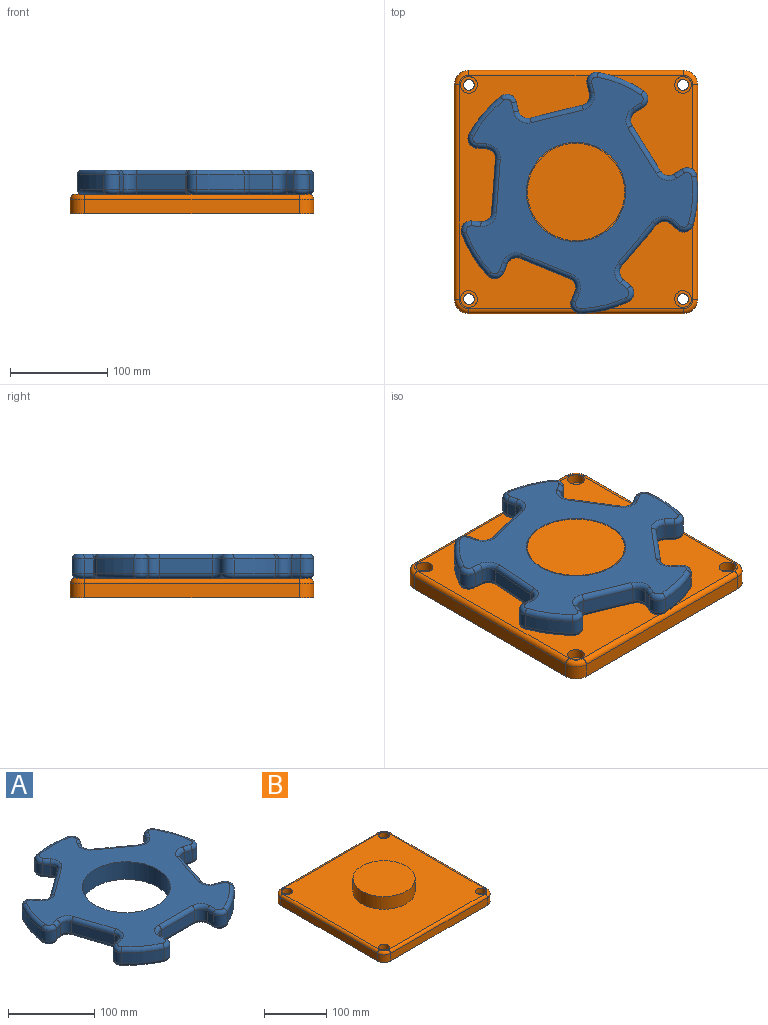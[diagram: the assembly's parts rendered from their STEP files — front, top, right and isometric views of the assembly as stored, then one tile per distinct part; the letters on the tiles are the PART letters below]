
ASSEMBLY  parts=2 mates=1
PART A: 123 faces, bbox 268.9x258.5x25 mm
  f0: plane 238.57x229.73mm, normal (0,0,1), area 21505.7mm2, adj f6,f43,f44,f45,f46,f47,f48,f49
  f1: plane 238.57x229.73mm, normal (0,0,-1), area 21505.7mm2, adj f6,f83,f84,f85,f86,f87,f88,f89
  f2: cylinder r=125mm len=40.68mm, axis (0,0,-1), area 759.5mm2, adj f13,f42,f51,f91
  f3: cylinder r=125mm len=47.82mm, axis (0,0,-1), area 759.5mm2, adj f35,f41,f67,f107
  f4: cylinder r=125mm len=50.29mm, axis (0,0,-1), area 759.5mm2, adj f28,f34,f82,f122
  f5: cylinder r=125mm len=47.82mm, axis (0,0,-1), area 759.5mm2, adj f21,f27,f66,f106
  f6: cylinder r=51mm len=102mm, axis (0,0,-1), area 8011.1mm2, adj f0,f1
  f7: cylinder r=125mm len=40.68mm, axis (0,0,-1), area 759.5mm2, adj f14,f20,f50,f90
  f8: plane 15x9.73mm, normal (-1,0,0), area 146mm2, adj f11,f14,f46,f86
  f9: plane 55x15mm, normal (0,-1,0), area 825mm2, adj f11,f12,f43,f83
  f10: plane 15x9.73mm, normal (1,0,0), area 146mm2, adj f12,f13,f47,f87
  f11: cylinder r=10mm len=15mm, axis (0,0,-1), area 235.6mm2, adj f8,f9,f44,f84
  f12: cylinder r=10mm len=15mm, axis (0,0,-1), area 235.6mm2, adj f9,f10,f45,f85
  f13: cylinder r=10mm len=15mm, axis (0,0,-1), area 299.5mm2, adj f2,f10,f49,f89
  f14: cylinder r=10mm len=15mm, axis (0,0,-1), area 299.5mm2, adj f7,f8,f48,f88
  f15: plane 15x9.26mm, normal (-0.31,-0.95,0), area 146mm2, adj f18,f21,f62,f102
  f16: plane 52.31x17mm, normal (0.95,-0.31,0), area 825mm2, adj f18,f19,f58,f98
  f17: plane 15x9.26mm, normal (0.31,0.95,0), area 146mm2, adj f19,f20,f54,f94
  f18: cylinder r=10mm len=15mm, axis (0,0,-1), area 235.6mm2, adj f15,f16,f60,f100
  f19: cylinder r=10mm len=15mm, axis (0,0,-1), area 235.6mm2, adj f16,f17,f56,f96
  f20: cylinder r=10mm len=16.25mm, axis (0,0,-1), area 299.5mm2, adj f7,f17,f52,f92
  f21: cylinder r=10mm len=15mm, axis (0,0,-1), area 299.5mm2, adj f5,f15,f64,f104
  f22: plane 15x7.87mm, normal (0.81,-0.59,0), area 146mm2, adj f25,f28,f78,f118
  f23: plane 44.5x32.33mm, normal (0.59,0.81,0), area 825mm2, adj f25,f26,f74,f114
  f24: plane 15x7.87mm, normal (-0.81,0.59,0), area 146mm2, adj f26,f27,f70,f110
  f25: cylinder r=10mm len=15mm, axis (0,0,-1), area 235.6mm2, adj f22,f23,f76,f116
  f26: cylinder r=10mm len=15mm, axis (0,0,-1), area 235.6mm2, adj f23,f24,f72,f112
  f27: cylinder r=10mm len=16.78mm, axis (0,0,-1), area 299.5mm2, adj f5,f24,f68,f108
  f28: cylinder r=10mm len=15.67mm, axis (0,0,-1), area 299.5mm2, adj f4,f22,f80,f120
  f29: plane 15x7.87mm, normal (0.81,0.59,0), area 146mm2, adj f32,f35,f71,f111
  f30: plane 44.5x32.33mm, normal (-0.59,0.81,0), area 825mm2, adj f32,f33,f75,f115
  f31: plane 15x7.87mm, normal (-0.81,-0.59,0), area 146mm2, adj f33,f34,f79,f119
  f32: cylinder r=10mm len=15mm, axis (0,0,-1), area 235.6mm2, adj f29,f30,f73,f113
  f33: cylinder r=10mm len=15mm, axis (0,0,-1), area 235.6mm2, adj f30,f31,f77,f117
  f34: cylinder r=10mm len=15.67mm, axis (0,0,-1), area 299.5mm2, adj f4,f31,f81,f121
  f35: cylinder r=10mm len=16.78mm, axis (0,0,-1), area 299.5mm2, adj f3,f29,f69,f109
  f36: plane 15x9.26mm, normal (-0.31,0.95,0), area 146mm2, adj f39,f42,f55,f95
  f37: plane 52.31x17mm, normal (-0.95,-0.31,0), area 825mm2, adj f39,f40,f59,f99
  f38: plane 15x9.26mm, normal (0.31,-0.95,0), area 146mm2, adj f40,f41,f63,f103
  f39: cylinder r=10mm len=15mm, axis (0,0,-1), area 235.6mm2, adj f36,f37,f57,f97
  f40: cylinder r=10mm len=15mm, axis (0,0,-1), area 235.6mm2, adj f37,f38,f61,f101
  f41: cylinder r=10mm len=15mm, axis (0,0,-1), area 299.5mm2, adj f3,f38,f65,f105
  f42: cylinder r=10mm len=16.25mm, axis (0,0,-1), area 299.5mm2, adj f2,f36,f53,f93
  f43: cylinder r=5mm len=55mm, axis (1,0,0), area 432mm2, adj f0,f9,f44,f45
  f44: torus R=15mm, axis (0,0,1), area 145.8mm2, adj f0,f11,f43,f46
  f45: torus R=15mm, axis (0,0,1), area 145.8mm2, adj f0,f12,f43,f47
  f46: cylinder r=5mm len=9.73mm, axis (0,-1,0), area 76.4mm2, adj f0,f8,f44,f48
  f47: cylinder r=5mm len=9.73mm, axis (0,1,0), area 76.4mm2, adj f0,f10,f45,f49
  f48: torus R=5mm, axis (0,0,1), area 128.3mm2, adj f0,f14,f46,f50
  f49: torus R=5mm, axis (0,0,1), area 128.3mm2, adj f0,f13,f47,f51
  f50: torus R=120mm, axis (0,0,1), area 391.9mm2, adj f0,f7,f48,f52
  f51: torus R=120mm, axis (0,0,1), area 391.9mm2, adj f0,f2,f49,f53
  f52: torus R=5mm, axis (0,0,1), area 128.3mm2, adj f0,f20,f50,f54
  f53: torus R=5mm, axis (0,0,1), area 128.3mm2, adj f0,f42,f51,f55
  f54: cylinder r=5mm len=10.8mm, axis (-0.95,0.31,0), area 76.4mm2, adj f0,f17,f52,f56
  f55: cylinder r=5mm len=10.8mm, axis (-0.95,-0.31,0), area 76.4mm2, adj f0,f36,f53,f57
  f56: torus R=15mm, axis (0,0,1), area 145.8mm2, adj f0,f19,f54,f58
  f57: torus R=15mm, axis (0,0,1), area 145.8mm2, adj f0,f39,f55,f59
  f58: cylinder r=5mm len=53.85mm, axis (0.31,0.95,0), area 432mm2, adj f0,f16,f56,f60
  f59: cylinder r=5mm len=53.85mm, axis (0.31,-0.95,0), area 432mm2, adj f0,f37,f57,f61
  f60: torus R=15mm, axis (0,0,1), area 145.8mm2, adj f0,f18,f58,f62
  f61: torus R=15mm, axis (0,0,1), area 145.8mm2, adj f0,f40,f59,f63
  f62: cylinder r=5mm len=10.8mm, axis (0.95,-0.31,0), area 76.4mm2, adj f0,f15,f60,f64
  f63: cylinder r=5mm len=10.8mm, axis (0.95,0.31,0), area 76.4mm2, adj f0,f38,f61,f65
  f64: torus R=5mm, axis (0,0,1), area 128.3mm2, adj f0,f21,f62,f66
  f65: torus R=5mm, axis (0,0,1), area 128.3mm2, adj f0,f41,f63,f67
  f66: torus R=120mm, axis (0,0,1), area 391.9mm2, adj f0,f5,f64,f68
  f67: torus R=120mm, axis (0,0,1), area 391.9mm2, adj f0,f3,f65,f69
  f68: torus R=5mm, axis (0,0,1), area 128.3mm2, adj f0,f27,f66,f70
  f69: torus R=5mm, axis (0,0,1), area 128.3mm2, adj f0,f35,f67,f71
  f70: cylinder r=5mm len=10.81mm, axis (-0.59,-0.81,0), area 76.4mm2, adj f0,f24,f68,f72
  f71: cylinder r=5mm len=10.81mm, axis (-0.59,0.81,0), area 76.4mm2, adj f0,f29,f69,f73
  f72: torus R=15mm, axis (0,0,1), area 145.8mm2, adj f0,f26,f70,f74
  f73: torus R=15mm, axis (0,0,1), area 145.8mm2, adj f0,f32,f71,f75
  f74: cylinder r=5mm len=47.44mm, axis (-0.81,0.59,0), area 432mm2, adj f0,f23,f72,f76
  f75: cylinder r=5mm len=47.44mm, axis (-0.81,-0.59,0), area 432mm2, adj f0,f30,f73,f77
  f76: torus R=15mm, axis (0,0,1), area 145.8mm2, adj f0,f25,f74,f78
  f77: torus R=15mm, axis (0,0,1), area 145.8mm2, adj f0,f33,f75,f79
  f78: cylinder r=5mm len=10.81mm, axis (0.59,0.81,0), area 76.4mm2, adj f0,f22,f76,f80
  f79: cylinder r=5mm len=10.81mm, axis (0.59,-0.81,0), area 76.4mm2, adj f0,f31,f77,f81
  f80: torus R=5mm, axis (0,0,1), area 128.3mm2, adj f0,f28,f78,f82
  f81: torus R=5mm, axis (0,0,1), area 128.3mm2, adj f0,f34,f79,f82
  f82: torus R=120mm, axis (0,0,1), area 391.9mm2, adj f0,f4,f80,f81
  f83: cylinder r=5mm len=55mm, axis (-1,0,0), area 432mm2, adj f1,f9,f84,f85
  f84: torus R=15mm, axis (0,0,1), area 145.8mm2, adj f1,f11,f83,f86
  f85: torus R=15mm, axis (0,0,1), area 145.8mm2, adj f1,f12,f83,f87
  f86: cylinder r=5mm len=9.73mm, axis (0,1,0), area 76.4mm2, adj f1,f8,f84,f88
  f87: cylinder r=5mm len=9.73mm, axis (0,-1,0), area 76.4mm2, adj f1,f10,f85,f89
  f88: torus R=5mm, axis (0,0,1), area 128.3mm2, adj f1,f14,f86,f90
  f89: torus R=5mm, axis (0,0,1), area 128.3mm2, adj f1,f13,f87,f91
  f90: torus R=120mm, axis (0,0,1), area 391.9mm2, adj f1,f7,f88,f92
  f91: torus R=120mm, axis (0,0,1), area 391.9mm2, adj f1,f2,f89,f93
  f92: torus R=5mm, axis (0,0,1), area 128.3mm2, adj f1,f20,f90,f94
  f93: torus R=5mm, axis (0,0,1), area 128.3mm2, adj f1,f42,f91,f95
  f94: cylinder r=5mm len=10.8mm, axis (0.95,-0.31,0), area 76.4mm2, adj f1,f17,f92,f96
  f95: cylinder r=5mm len=10.8mm, axis (0.95,0.31,0), area 76.4mm2, adj f1,f36,f93,f97
  f96: torus R=15mm, axis (0,0,1), area 145.8mm2, adj f1,f19,f94,f98
  f97: torus R=15mm, axis (0,0,1), area 145.8mm2, adj f1,f39,f95,f99
  f98: cylinder r=5mm len=53.85mm, axis (-0.31,-0.95,0), area 432mm2, adj f1,f16,f96,f100
  f99: cylinder r=5mm len=53.85mm, axis (-0.31,0.95,0), area 432mm2, adj f1,f37,f97,f101
  f100: torus R=15mm, axis (0,0,1), area 145.8mm2, adj f1,f18,f98,f102
  f101: torus R=15mm, axis (0,0,1), area 145.8mm2, adj f1,f40,f99,f103
  f102: cylinder r=5mm len=10.8mm, axis (-0.95,0.31,0), area 76.4mm2, adj f1,f15,f100,f104
  f103: cylinder r=5mm len=10.8mm, axis (-0.95,-0.31,0), area 76.4mm2, adj f1,f38,f101,f105
  f104: torus R=5mm, axis (0,0,1), area 128.3mm2, adj f1,f21,f102,f106
  f105: torus R=5mm, axis (0,0,1), area 128.3mm2, adj f1,f41,f103,f107
  f106: torus R=120mm, axis (0,0,1), area 391.9mm2, adj f1,f5,f104,f108
  f107: torus R=120mm, axis (0,0,1), area 391.9mm2, adj f1,f3,f105,f109
  f108: torus R=5mm, axis (0,0,1), area 128.3mm2, adj f1,f27,f106,f110
  f109: torus R=5mm, axis (0,0,1), area 128.3mm2, adj f1,f35,f107,f111
  f110: cylinder r=5mm len=10.81mm, axis (0.59,0.81,0), area 76.4mm2, adj f1,f24,f108,f112
  f111: cylinder r=5mm len=10.81mm, axis (0.59,-0.81,0), area 76.4mm2, adj f1,f29,f109,f113
  f112: torus R=15mm, axis (0,0,1), area 145.8mm2, adj f1,f26,f110,f114
  f113: torus R=15mm, axis (0,0,1), area 145.8mm2, adj f1,f32,f111,f115
  f114: cylinder r=5mm len=47.44mm, axis (0.81,-0.59,0), area 432mm2, adj f1,f23,f112,f116
  f115: cylinder r=5mm len=47.44mm, axis (0.81,0.59,0), area 432mm2, adj f1,f30,f113,f117
  f116: torus R=15mm, axis (0,0,1), area 145.8mm2, adj f1,f25,f114,f118
  f117: torus R=15mm, axis (0,0,1), area 145.8mm2, adj f1,f33,f115,f119
  f118: cylinder r=5mm len=10.81mm, axis (-0.59,-0.81,0), area 76.4mm2, adj f1,f22,f116,f120
  f119: cylinder r=5mm len=10.81mm, axis (-0.59,0.81,0), area 76.4mm2, adj f1,f31,f117,f121
  f120: torus R=5mm, axis (0,0,1), area 128.3mm2, adj f1,f28,f118,f122
  f121: torus R=5mm, axis (0,0,1), area 128.3mm2, adj f1,f34,f119,f122
  f122: torus R=120mm, axis (0,0,1), area 391.9mm2, adj f1,f4,f120,f121
PART B: 32 faces, bbox 252.5x252.5x45 mm
  f0: plane 220x15mm, normal (1,0,0), area 3300mm2, adj f5,f8,f11,f27
  f1: plane 220x15mm, normal (0,1,0), area 3300mm2, adj f5,f8,f9,f31
  f2: plane 220x15mm, normal (-1,0,0), area 3300mm2, adj f5,f9,f10,f28
  f3: plane 220x15mm, normal (0,-1,0), area 3300mm2, adj f5,f10,f11,f24
  f4: plane 240x240mm, normal (0,0,1), area 48725.4mm2, adj f6,f14,f17,f20,f23,f24,f25,f26
  f5: plane 250x250mm, normal (0,0,-1), area 61926.7mm2, adj f0,f1,f2,f3,f8,f9,f10,f11
  f6: cylinder r=50mm len=100mm, axis (0,0,-1), area 7854mm2, adj f4,f7
  f7: plane 100x100mm, normal (0,0,1), area 7854mm2, adj f6
  f8: cylinder r=15mm len=15mm, axis (0,0,-1), area 353.4mm2, adj f0,f1,f5,f29
  f9: cylinder r=15mm len=15mm, axis (0,0,1), area 353.4mm2, adj f1,f2,f5,f30
  f10: cylinder r=15mm len=15mm, axis (0,0,-1), area 353.4mm2, adj f2,f3,f5,f26
  f11: cylinder r=15mm len=15mm, axis (0,0,1), area 353.4mm2, adj f0,f3,f5,f25
  f12: cylinder r=5.5mm len=11mm, axis (0,0,1), area 345.6mm2, adj f5,f13
  f13: plane 17.25x17.25mm, normal (0,0,1), area 138.7mm2, adj f12,f14
  f14: cylinder r=8.62mm len=17.25mm, axis (0,0,1), area 541.9mm2, adj f4,f13
  f15: cylinder r=5.5mm len=11mm, axis (0,0,1), area 345.6mm2, adj f5,f16
  f16: plane 17.25x17.25mm, normal (0,0,1), area 138.7mm2, adj f15,f17
  f17: cylinder r=8.62mm len=17.25mm, axis (0,0,1), area 541.9mm2, adj f4,f16
  f18: cylinder r=5.5mm len=11mm, axis (0,0,1), area 345.6mm2, adj f5,f19
  f19: plane 17.25x17.25mm, normal (0,0,1), area 138.7mm2, adj f18,f20
  f20: cylinder r=8.62mm len=17.25mm, axis (0,0,1), area 541.9mm2, adj f4,f19
  f21: cylinder r=5.5mm len=11mm, axis (0,0,1), area 345.6mm2, adj f5,f22
  f22: plane 17.25x17.25mm, normal (0,0,1), area 138.7mm2, adj f21,f23
  f23: cylinder r=8.62mm len=17.25mm, axis (0,0,1), area 541.9mm2, adj f4,f22
  f24: cylinder r=5mm len=220mm, axis (-1,0,0), area 1727.9mm2, adj f3,f4,f25,f26
  f25: torus R=10mm, axis (0,0,1), area 162.6mm2, adj f4,f11,f24,f27
  f26: torus R=10mm, axis (0,0,1), area 162.6mm2, adj f4,f10,f24,f28
  f27: cylinder r=5mm len=220mm, axis (0,-1,0), area 1727.9mm2, adj f0,f4,f25,f29
  f28: cylinder r=5mm len=220mm, axis (0,1,0), area 1727.9mm2, adj f2,f4,f26,f30
  f29: torus R=10mm, axis (0,0,1), area 162.6mm2, adj f4,f8,f27,f31
  f30: torus R=10mm, axis (0,0,1), area 162.6mm2, adj f4,f9,f28,f31
  f31: cylinder r=5mm len=220mm, axis (1,0,0), area 1727.9mm2, adj f1,f4,f29,f30
PLACE A rot(axis=(0,0,-1),22.2deg) t=(0,0,0)mm
PLACE B at identity fixed
MATE revolute A.f2 <-> B.f6  axis (0,0,1) through (0,0,45)mm
